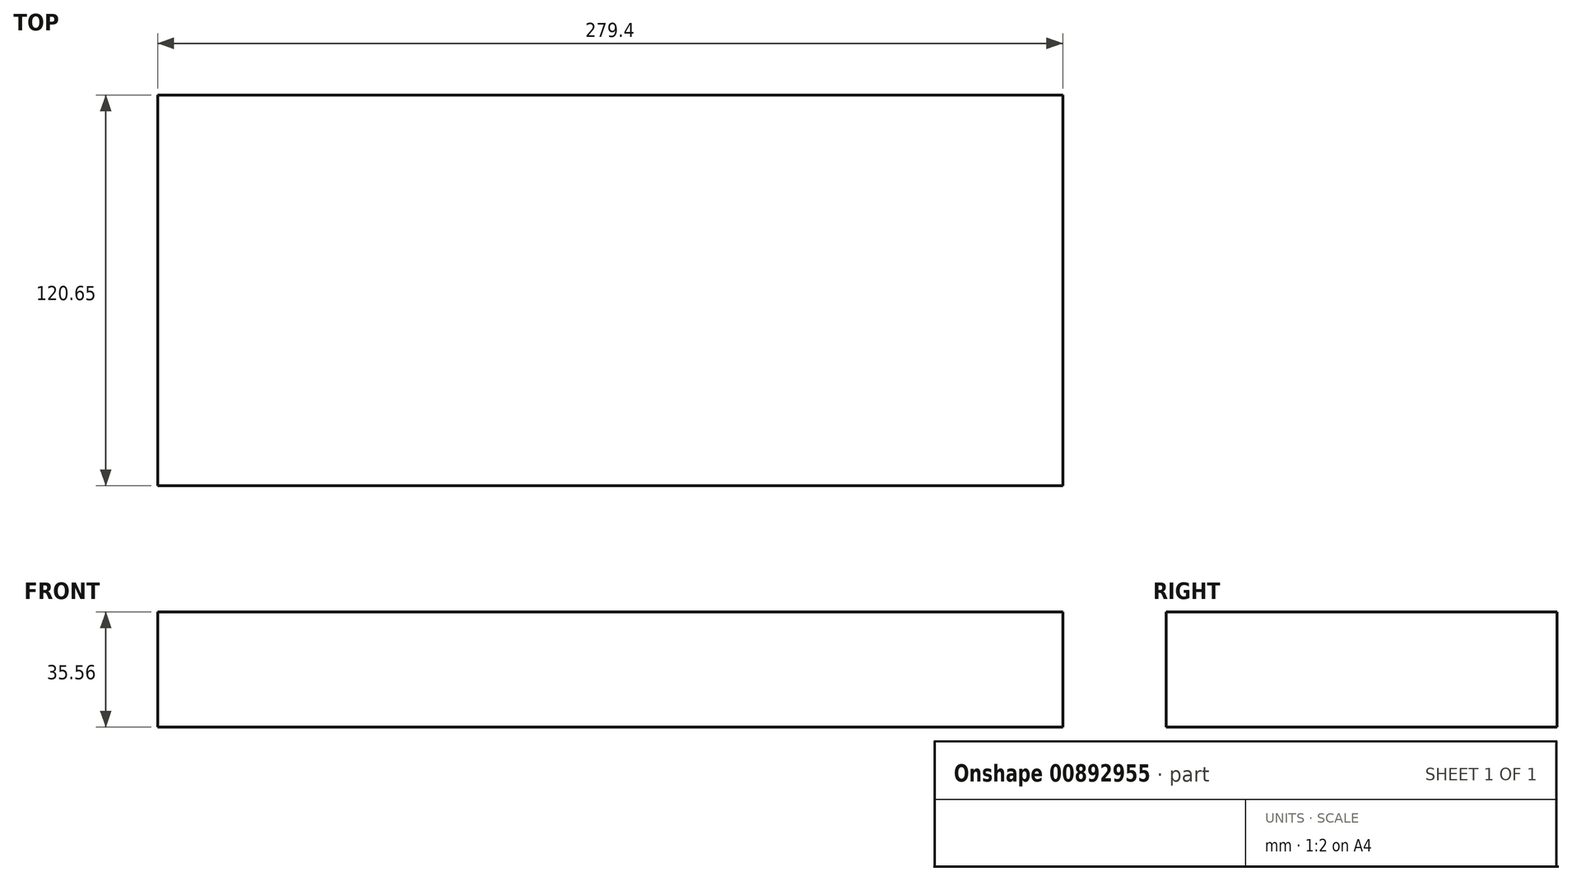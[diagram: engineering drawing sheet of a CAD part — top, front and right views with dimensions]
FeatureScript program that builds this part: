
annotation { "Feature Type Name" : "Feature", "Feature Type Description" : "" }
export const myFeature = defineFeature(function(context is Context, id is Id, definition is map)
    precondition{}
    {
        {
            var Q0;
            Q0=qCreatedBy(makeId("Top.planeOp"),FACE);
            var sketch = newSketch(context, id + "F0", { "sketchPlane" : qUnion([Q0])});
            skLineSegment(sketch, "E0.bottom", {"start": v(0, 0) * mm, "end": v(279.4, 0) * mm});
            skLineSegment(sketch, "E0.top", {"start": v(0, 120.65) * mm, "end": v(279.4, 120.65) * mm});
            skLineSegment(sketch, "E0.left", {"start": v(0, 0) * mm, "end": v(0, 120.65) * mm});
            skLineSegment(sketch, "E0.right", {"start": v(279.4, 0) * mm, "end": v(279.4, 120.65) * mm});
            skSolve(sketch);
        }
        {
            var Q0;
            Q0 = qSketchRegion(id + "F0", true);
            extrude(context, id + "F1", {"entities" : qUnion([Q0]), "depth" : 35.56 * mm, "offsetDistance" : 25.4 * mm});
        }
    });
